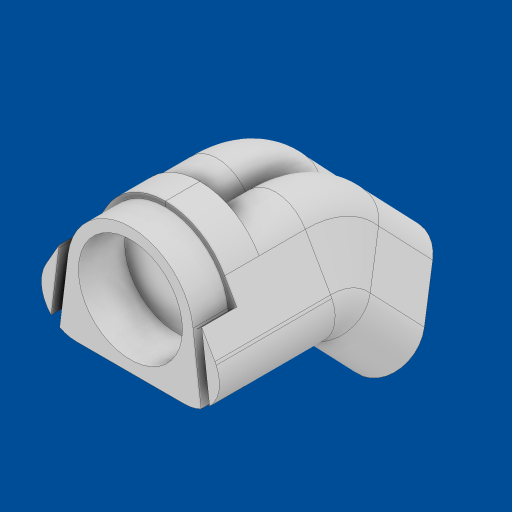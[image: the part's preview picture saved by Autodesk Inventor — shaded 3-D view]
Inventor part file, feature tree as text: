
AUTODESK INVENTOR PART (.ipt)
format: ipt  version: 2023 (Build 270158000, 158)  size: 561,664 bytes
history: native  units: mm
features: extrude x12, sketch x10, plane x3, chamfer x2, mirror x1, revolve x1
ambient origin geometry x8: Origin, YZ Plane, XZ Plane, XY Plane, X Axis, Y Axis, Z Axis, Center Point
bodies: Solid1 (feature_tree)
feature tree (29):
  sketch  "Sketch1"  dims[d0=100.0mm d1=25.0mm d2=7.5mm d3=7.5mm d4=60.0deg d5=15.0mm d6=11.0mm d7=11.0mm d8=15.0mm d14=4.0mm d15=0.0mm]
  extrude  "Extrusion1"  Depth=15.0mm TaperAngle=0.0deg
  plane  "Work Plane13"
  sketch  "Sketch7"  dims[d72=7.5mm d73=90.0deg]
  extrude  "Extrusion6"  TaperAngle=90.0deg  [1 undecoded]
  extrude  "Extrusion7"  Depth=7.5mm
  mirror  "Mirror4"
  plane  "Work Plane9"
  extrude  "Extrusion8"  Depth=15.0mm
  revolve  "Revolution2"  [1 undecoded]
  extrude  "Extrusion9"  Depth=6.5mm
  extrude  "Extrusion10"  Depth=15.0mm TaperAngle=0.0deg
  extrude  "Extrusion11"  Depth=10.0mm TaperAngle=0.0deg
  chamfer  "Chamfer3"  Distance=4.0mm
  chamfer  "Chamfer4"  Distance=10.0mm
  plane  "Work Plane16"
  extrude  "Extrusion14"  Depth=15.0mm TaperAngle=45.0deg
  extrude  "Extrusion21"  Depth=15.0mm TaperAngle=45.0deg
  extrude  "Extrusion25"  Depth=15.0mm
  extrude  "Extrusion28"  Depth=15.0mm
  extrude  "Extrusion30"  Depth=15.0mm
  sketch  "Sketch14"  dims[d74=7.5mm d75=5.5mm]
  sketch  "Sketch15"  dims[d76=5.5mm d77=15.0mm]
  sketch  "Sketch19"  dims[d78=11.0mm d79=11.0mm]
  sketch  "Sketch23"  dims[d80=2.0mm d81=6.5mm]
  sketch  "Sketch24"  dims[d82=6.5mm d83=15.0mm d84=0.0mm]
  sketch  "Sketch34"  dims[d93=10.0mm d94=0.0mm d115=20.0mm d116=0.0mm]
  sketch  "Sketch35"  dims[d131=8.648979mm d132=4.0mm d133=0.0mm d134=10.0mm d135=0.0mm]
  sketch  "Sketch37"  dims[d136=10.0mm d137=0.0mm d138=2.0mm d139=4.0mm d140=45.0deg d141=2.0mm d142=4.0mm d143=45.0deg d153=15.0mm d154=15.0mm d155=15.0mm d156=25.0mm d157=0.0mm d222=45.0mm d243=1.0mm d244=27.222586mm d245=15.0mm d246=0.0mm d266=261.822mm d267=7.45mm d268=27.223mm d269=1.0mm d270=35.0mm d271=100.0mm d272=2.0mm d273=1.1mm d274=180.0deg d275=1.0mm d276=15.709295mm d277=7.55mm d278=0.0mm d279=2.0mm d280=1.0mm d281=180.0deg d301=0.0mm d302=22.5mm d303=10.0mm d304=0.0mm d305=10.0mm d306=5.0mm d312=10.0mm d313=15.0mm d314=0.0mm d182=0.5mm d183=0.872665mm d184=0.5mm d185=0.872665mm d224=0.5mm d225=0.872665mm d226=0.5mm d227=0.872665mm d258=0.5mm d259=0.872665mm d260=0.5mm d261=0.872665mm]
note: 2 required parameter values undecoded (feature->parameter linkage not recoverable at this tier; creation-order binding heuristic only, values carry confidence <= 0.55)